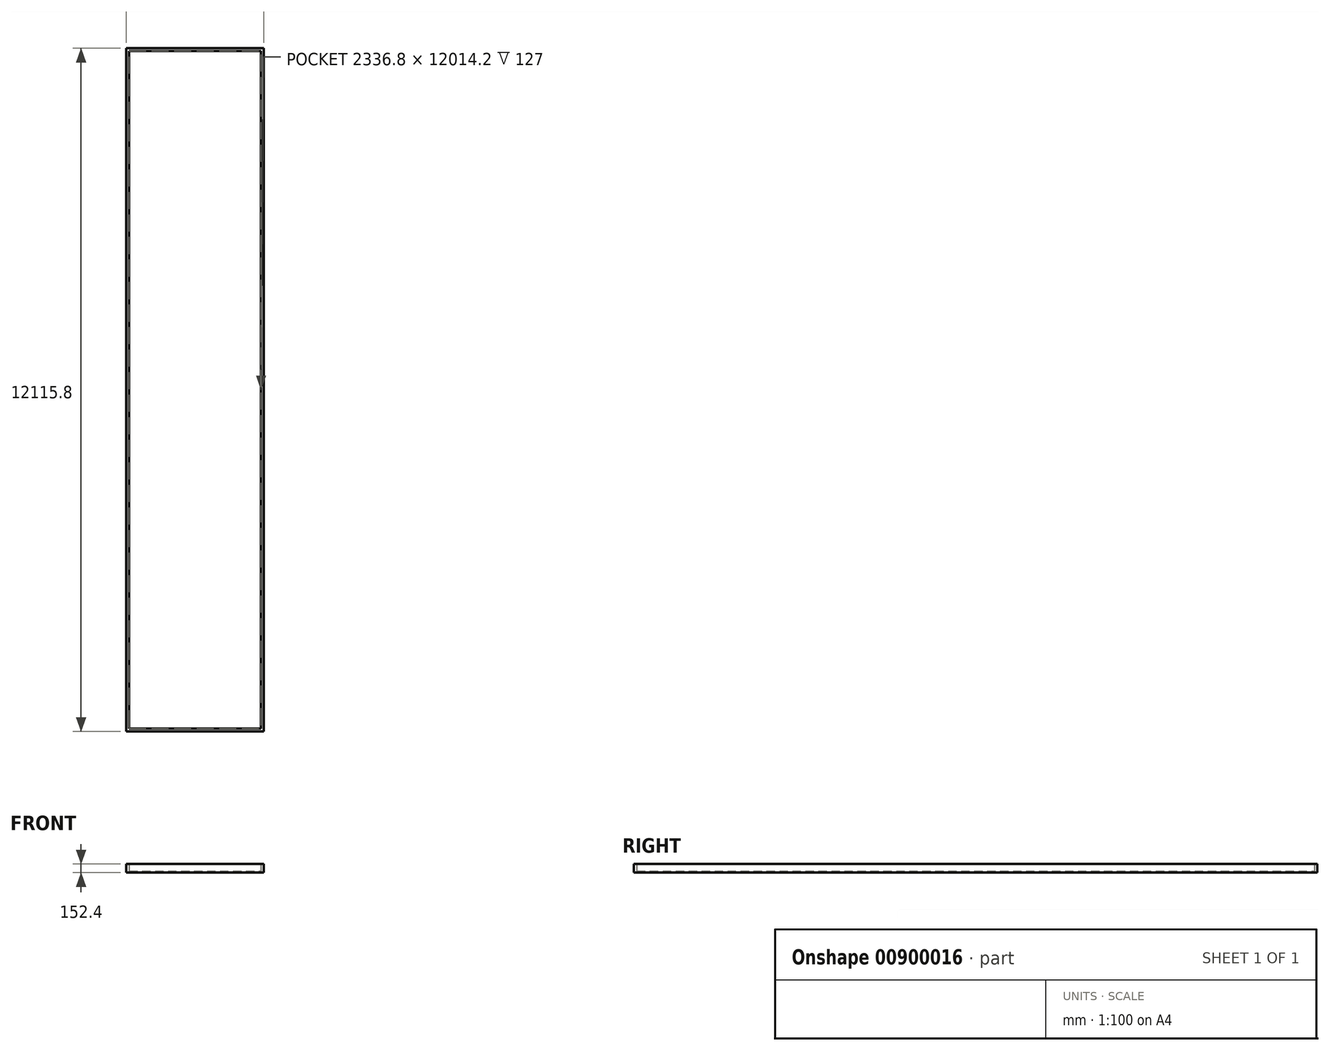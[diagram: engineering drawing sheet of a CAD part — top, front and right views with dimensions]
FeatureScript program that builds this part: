
annotation { "Feature Type Name" : "Feature", "Feature Type Description" : "" }
export const myFeature = defineFeature(function(context is Context, id is Id, definition is map)
    precondition{}
    {
        {
            var Q0;
            Q0=qCreatedBy(makeId("Top.planeOp"),FACE);
            var sketch = newSketch(context, id + "F0", { "sketchPlane" : qUnion([Q0])});
            skLineSegment(sketch, "E0.bottom", {"start": v(-1480.2, -6375.4) * mm, "end": v(856.6, -6375.4) * mm});
            skLineSegment(sketch, "E0.top", {"start": v(-1480.2, 5638.8) * mm, "end": v(856.6, 5638.8) * mm});
            skLineSegment(sketch, "E0.left", {"start": v(-1480.2, -6375.4) * mm, "end": v(-1480.2, 5638.8) * mm});
            skLineSegment(sketch, "E0.right", {"start": v(856.6, -6375.4) * mm, "end": v(856.6, 5638.8) * mm});
            skLineSegment(sketch, "E1.bottom", {"start": v(856.6, 5638.8) * mm, "end": v(-1480.2, 5638.8) * mm});
            skLineSegment(sketch, "E1.top", {"start": v(856.6, 3810) * mm, "end": v(-1480.2, 3810) * mm});
            skLineSegment(sketch, "E1.left", {"start": v(856.6, 5638.8) * mm, "end": v(856.6, 3810) * mm});
            skLineSegment(sketch, "E1.right", {"start": v(-1480.2, 5638.8) * mm, "end": v(-1480.2, 3810) * mm});
            skLineSegment(sketch, "E2.bottom", {"start": v(-1480.2, 3810) * mm, "end": v(856.6, 3810) * mm});
            skLineSegment(sketch, "E2.top", {"start": v(-1480.2, 3657.6) * mm, "end": v(856.6, 3657.6) * mm});
            skLineSegment(sketch, "E2.left", {"start": v(-1480.2, 3810) * mm, "end": v(-1480.2, 3657.6) * mm});
            skLineSegment(sketch, "E2.right", {"start": v(856.6, 3810) * mm, "end": v(856.6, 3657.6) * mm});
            skLineSegment(sketch, "E3.top", {"start": v(-1480.2, 0) * mm, "end": v(856.6, 0) * mm});
            skLineSegment(sketch, "E3.left", {"start": v(-1480.2, 3657.6) * mm, "end": v(-1480.2, 0) * mm});
            skLineSegment(sketch, "E3.right", {"start": v(856.6, 3657.6) * mm, "end": v(856.6, 0) * mm});
            skLineSegment(sketch, "E4.top", {"start": v(-1480.2, -152.4) * mm, "end": v(856.6, -152.4) * mm});
            skLineSegment(sketch, "E4.left", {"start": v(-1480.2, 0) * mm, "end": v(-1480.2, -152.4) * mm});
            skLineSegment(sketch, "E4.right", {"start": v(856.6, 0) * mm, "end": v(856.6, -152.4) * mm});
            skLineSegment(sketch, "E5.top", {"start": v(-1480.2, -3937) * mm, "end": v(856.6, -3937) * mm});
            skLineSegment(sketch, "E5.left", {"start": v(-1480.2, -6375.4) * mm, "end": v(-1480.2, -3937) * mm});
            skLineSegment(sketch, "E5.right", {"start": v(856.6, -6375.4) * mm, "end": v(856.6, -3937) * mm});
            skLineSegment(sketch, "E6.top", {"start": v(-1480.2, -3784.6) * mm, "end": v(856.6, -3784.6) * mm});
            skLineSegment(sketch, "E6.left", {"start": v(-1480.2, -3937) * mm, "end": v(-1480.2, -3784.6) * mm});
            skLineSegment(sketch, "E6.right", {"start": v(856.6, -3937) * mm, "end": v(856.6, -3784.6) * mm});
            skLineSegment(sketch, "E7.bottom", {"start": v(-1531, 5689.6) * mm, "end": v(907.4, 5689.6) * mm});
            skLineSegment(sketch, "E7.top", {"start": v(-1531, -6426.2) * mm, "end": v(907.4, -6426.2) * mm});
            skLineSegment(sketch, "E7.left", {"start": v(-1531, 5689.6) * mm, "end": v(-1531, -6426.2) * mm});
            skLineSegment(sketch, "E7.right", {"start": v(907.4, 5689.6) * mm, "end": v(907.4, -6426.2) * mm});
            skSolve(sketch);
        }
        {
            var Q0;
            Q0=makeQuery(id+"F0.imprint","IMPRINT",FACE,{"disambiguationData":[TD([[makeQuery(id+"F0.imprint","IMPRINT",EDGE,{"derivedFrom":sQuery(id+"F0.wireOp",EDGE,"E0.left")}),1.0]])]});
            var Q1;
            Q1=makeQuery(id+"F0.imprint","IMPRINT",FACE,{"disambiguationData":[TD([[makeQuery(id+"F0.imprint","IMPRINT",EDGE,{"derivedFrom":sQuery(id+"F0.wireOp",EDGE,"E2.bottom")}),-1.0]])]});
            var Q2;
            Q2=makeQuery(id+"F0.imprint","IMPRINT",FACE,{"disambiguationData":[TD([[makeQuery(id+"F0.imprint","IMPRINT",EDGE,{"derivedFrom":sQuery(id+"F0.wireOp",EDGE,"E3.top")}),-1.0]])]});
            var Q3;
            Q3=makeQuery(id+"F0.imprint","IMPRINT",FACE,{"disambiguationData":[TD([[makeQuery(id+"F0.imprint","IMPRINT",EDGE,{"derivedFrom":sQuery(id+"F0.wireOp",EDGE,"E5.top")}),1.0]])]});
            extrude(context, id + "F1", {"entities" : qUnion([Q0, Q1, Q2, Q3]), "depth" : 152.4 * mm, "offsetDistance" : 25.4 * mm});
        }
        {
            var Q0;
            Q0=makeQuery(id+"F0.imprint","IMPRINT",FACE,{"disambiguationData":[TD([[makeQuery(id+"F0.imprint","IMPRINT",EDGE,{"derivedFrom":sQuery(id+"F0.wireOp",EDGE,"E1.bottom")}),1.0]])]});
            var Q1;
            Q1=makeQuery(id+"F0.imprint","IMPRINT",FACE,{"disambiguationData":[TD([[makeQuery(id+"F0.imprint","IMPRINT",EDGE,{"derivedFrom":sQuery(id+"F0.wireOp",EDGE,"E2.top")}),-1.0]])]});
            var Q2;
            Q2=makeQuery(id+"F0.imprint","IMPRINT",FACE,{"disambiguationData":[TD([[makeQuery(id+"F0.imprint","IMPRINT",EDGE,{"derivedFrom":sQuery(id+"F0.wireOp",EDGE,"E0.left")}),-1.0]])]});
            var Q3;
            Q3=makeQuery(id+"F0.imprint","IMPRINT",FACE,{"disambiguationData":[TD([[makeQuery(id+"F0.imprint","IMPRINT",EDGE,{"derivedFrom":sQuery(id+"F0.wireOp",EDGE,"E0.bottom")}),1.0]])]});
            extrude(context, id + "F2", {"entities" : qUnion([Q0, Q1, Q2, Q3]), "operationType" : NewBodyOperationType.ADD, "depth" : 25.4 * mm, "offsetDistance" : 25.4 * mm});
        }
    });
